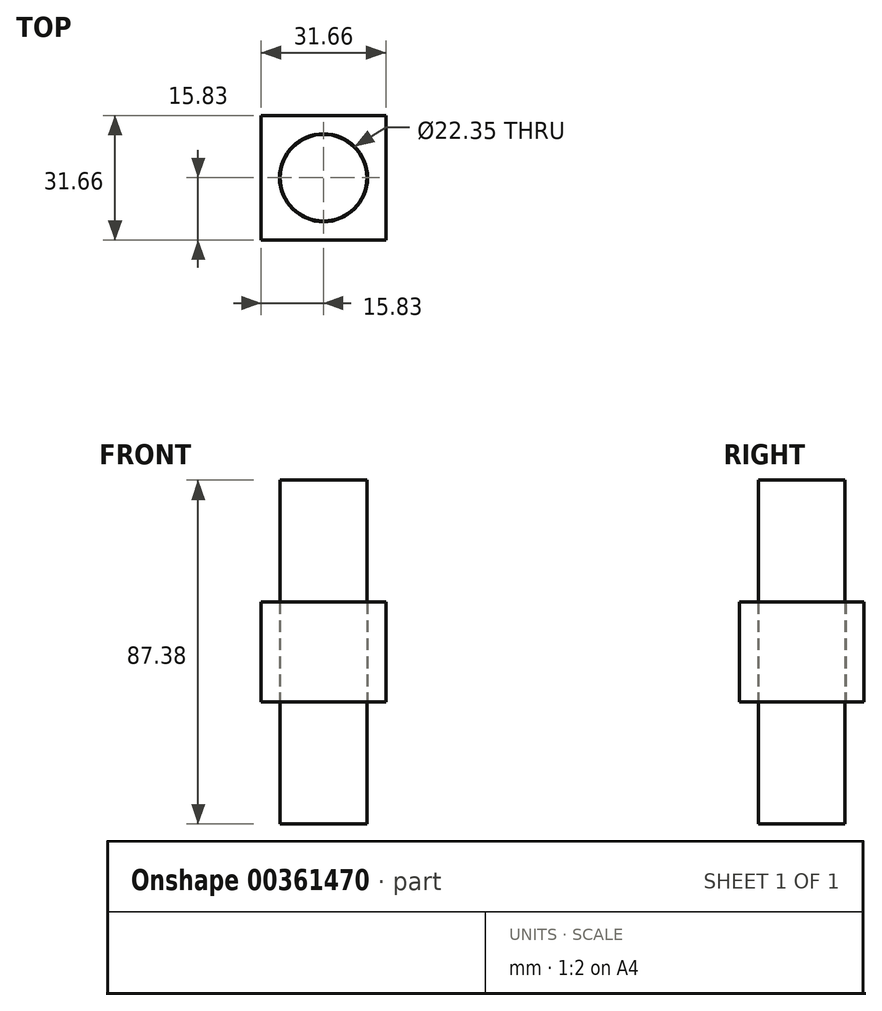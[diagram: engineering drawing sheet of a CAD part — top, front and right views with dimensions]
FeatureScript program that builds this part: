
annotation { "Feature Type Name" : "Feature", "Feature Type Description" : "" }
export const myFeature = defineFeature(function(context is Context, id is Id, definition is map)
    precondition{}
    {
        {
            var Q0;
            Q0=qCreatedBy(makeId("Top.planeOp"),FACE);
            var sketch = newSketch(context, id + "F0", { "sketchPlane" : qUnion([Q0])});
            skLineSegment(sketch, "E0.bottom", {"start": v(15.83, -15.83) * mm, "end": v(-15.83, -15.83) * mm});
            skLineSegment(sketch, "E0.top", {"start": v(15.83, 15.83) * mm, "end": v(-15.83, 15.83) * mm});
            skLineSegment(sketch, "E0.left", {"start": v(15.83, -15.83) * mm, "end": v(15.83, 15.83) * mm});
            skLineSegment(sketch, "E0.right", {"start": v(-15.83, -15.83) * mm, "end": v(-15.83, 15.83) * mm});
            skPoint(sketch, "E0.middle", {"position": v(0, 0) * mm});
            skCircle(sketch, "E1", {"center": v(0, 0) * mm, "radius": 11.18 * mm});
            skSolve(sketch);
        }
        {
            var Q0;
            Q0=makeQuery(id+"F0.imprint","IMPRINT",FACE,{"disambiguationData":[TD([[makeQuery(id+"F0.imprint","IMPRINT",EDGE,{"derivedFrom":sQuery(id+"F0.wireOp",EDGE,"E0.bottom")}),-1.0]])]});
            extrude(context, id + "F1", {"entities" : qUnion([Q0]), "endBound" : BoundingType.SYMMETRIC, "depth" : 25.4 * mm});
        }
        {
            var Q0;
            Q0=qCreatedBy(makeId("Top.planeOp"),FACE);
            var sketch = newSketch(context, id + "F2", { "sketchPlane" : qUnion([Q0])});
            skCircle(sketch, "E2", {"center": v(0, 0) * mm, "radius": 11 * mm});
            skSolve(sketch);
        }
        {
            var Q0;
            Q0=makeQuery(id+"F2.imprint","IMPRINT",FACE,{"disambiguationData":[TD([[makeQuery(id+"F2.imprint","IMPRINT",EDGE,{"derivedFrom":sQuery(id+"F2.wireOp",EDGE,"E2")}),1.0]])]});
            extrude(context, id + "F3", {"entities" : qUnion([Q0]), "endBound" : BoundingType.SYMMETRIC, "depth" : 87.38 * mm});
        }
    });
